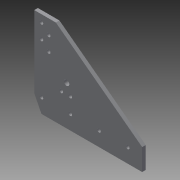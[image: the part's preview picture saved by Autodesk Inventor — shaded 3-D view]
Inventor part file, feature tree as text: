
AUTODESK INVENTOR PART (.ipt)
format: ipt  version: 2015 SP1 (Build 190203100, 203)  size: 140,288 bytes
history: native  units: in
note: dims shown in document units (in); Inventor stores cm internally (conversion verified against a paired STEP export)
features: extrude x3, sketch x3
ambient origin geometry x8: Origin, YZ Plane, XZ Plane, XY Plane, X Axis, Y Axis, Z Axis, Center Point
bodies: Body1 (feature_tree)
feature tree (6):
  extrude  "Extrusion4"  Depth=6.0in
  extrude  "Extrusion5"  Depth=2.0in
  extrude  "Extrusion6"  Depth=0.25in
  sketch  "Sketch1"  dims[d0=7.5in d1=6.0in]
  sketch  "Sketch3"  dims[d2=0.5in d3=2.0in]
  sketch  "Sketch4"  dims[d8=1.0in d9=1.0in d10=1.5in d11=90.0deg d12=1.5in d13=90.0deg d14=6.0in d15=180.0deg d16=1.5in d17=0.5in d18=0.5in d19=0.5in d20=0.5in d21=0.5in d22=1.0in d23=1.5in d24=2.0in d25=0.25in d26=0.25in d29=0.25in d30=0.25in d31=0.25in d32=0.25in d35=2.0in d36=2.0in d38=0.25in d39=0.25in d46=1.0in d47=1.0in d48=0.25in d49=0.0in d50=1.0in d51=0.5in d52=0.25in d53=0.0in d54=0.375in d55=1.0in d56=2.0625in d57=2.0625in d58=2.75in d59=0.75in d60=0.25in d61=0.25in d62=0.375in d63=0.25in d64=0.0in]
